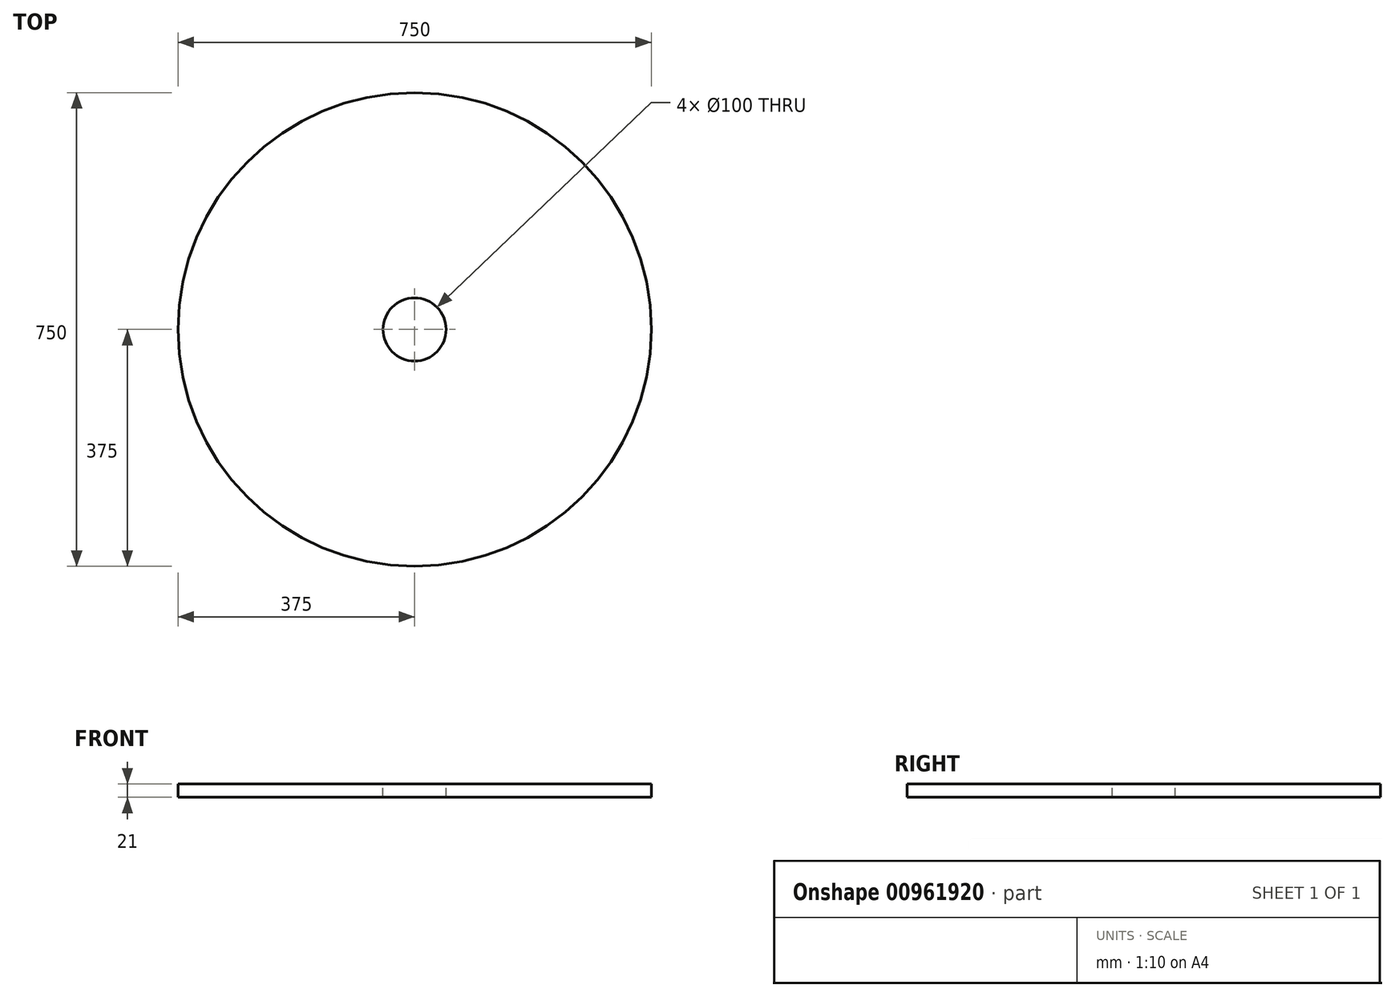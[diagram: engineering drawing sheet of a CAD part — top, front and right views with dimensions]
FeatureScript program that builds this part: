
annotation { "Feature Type Name" : "Feature", "Feature Type Description" : "" }
export const myFeature = defineFeature(function(context is Context, id is Id, definition is map)
    precondition{}
    {
        {
            var Q0;
            Q0=qCreatedBy(makeId("Top.planeOp"),FACE);
            var sketch = newSketch(context, id + "F0", { "sketchPlane" : qUnion([Q0])});
            skCircle(sketch, "E0", {"center": v(0, 0) * mm, "radius": 375 * mm});
            skSolve(sketch);
        }
        {
            var Q0;
            Q0=makeQuery(id+"F0.imprint","IMPRINT",FACE,{"disambiguationData":[TD([[makeQuery(id+"F0.imprint","IMPRINT",EDGE,{"derivedFrom":sQuery(id+"F0.wireOp",EDGE,"E0")}),1.0]])]});
            extrude(context, id + "F1", {"entities" : qUnion([Q0]), "oppositeDirection" : true, "depth" : 21 * mm, "offsetDistance" : 25.4 * mm});
        }
        {
            var Q0;
            Q0=makeQuery(id+"F1.opExtrude","CAP_FACE",FACE,{"disambiguationData":[OSD([sQuery(id+"F0.wireOp",EDGE,"E0")])],"isStart":true});
            var sketch = newSketch(context, id + "F2", { "sketchPlane" : qUnion([Q0])});
            skCircle(sketch, "E1", {"center": v(0, 0) * mm, "radius": 50 * mm});
            skSolve(sketch);
        }
        {
            var Q0;
            Q0=sQuery(id+"F2.wireOp",VERTEX,"E1.center");
            var Q1;
            Q1=makeQuery(id+"F1.opExtrude","SWEPT_BODY",BODY,{"disambiguationData":[OSD([sQuery(id+"F0.wireOp",EDGE,"E0")])]});
            hole(context, id + "F3", {"style" : HoleStyle.SIMPLE, "endStyle" : HoleEndStyle.THROUGH, "holeDiameter" : 100 * mm, "majorDiameter" : 6.35 * mm, "isTappedThrough" : true, "tappedDepth" : 12.7 * mm, "tapClearance" : 3, "locations" : qUnion([Q0]), "scope" : qUnion([Q1])});
        }
    });
